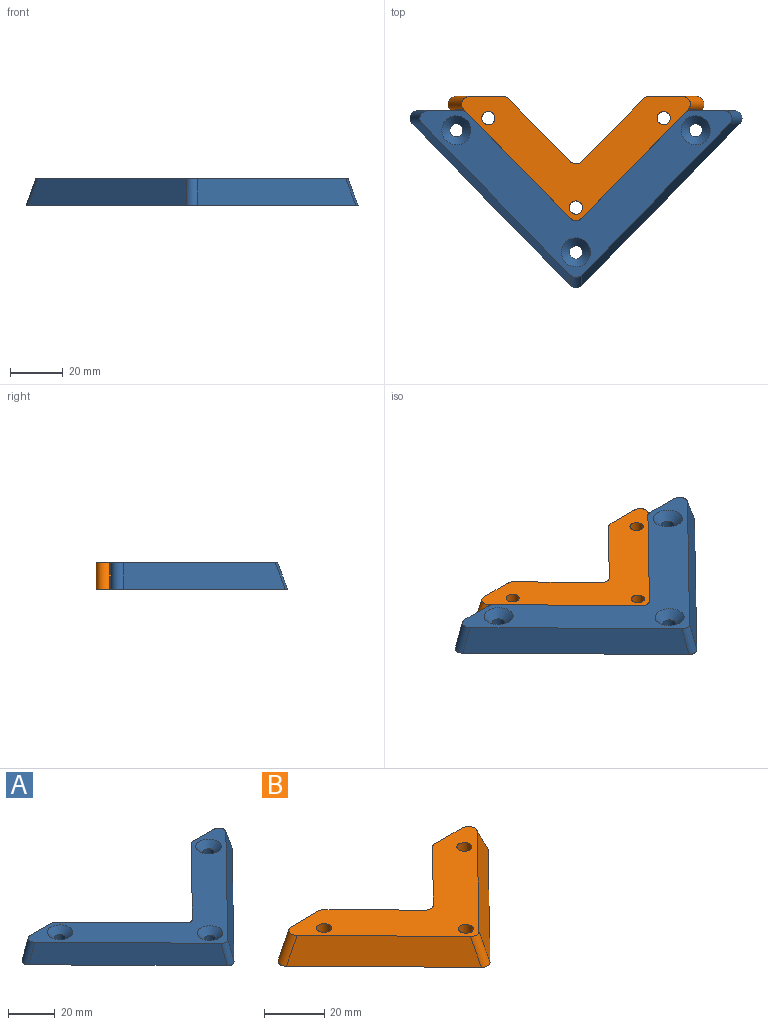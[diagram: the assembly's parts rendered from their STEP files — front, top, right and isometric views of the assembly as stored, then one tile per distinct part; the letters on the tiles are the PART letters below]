
ASSEMBLY  parts=2 mates=1
PART A: 20 faces, bbox 125.3x66.9x12.1 mm
  f0: plane 44.97x44.07mm, normal (-0.67,0.66,-0.34), area 631.3mm2, adj f9,f10,f14,f19
  f1: plane 44.97x44.07mm, normal (0.67,0.66,-0.34), area 631.3mm2, adj f9,f10,f14,f15
  f2: plane 15.93x10mm, normal (0,1,0), area 115.1mm2, adj f9,f10,f15,f16
  f3: plane 60.98x59.75mm, normal (-0.69,-0.68,0.26), area 856.1mm2, adj f9,f10,f16,f17
  f4: plane 60.98x59.75mm, normal (0.69,-0.68,0.26), area 856.1mm2, adj f9,f10,f17,f18
  f5: cylinder r=2.5mm len=7mm, axis (0,0,-1), area 110mm2, adj f10,f13
  f6: cylinder r=2.5mm len=7mm, axis (0,0,-1), area 110mm2, adj f10,f12
  f7: cylinder r=2.5mm len=7mm, axis (0,0,-1), area 110mm2, adj f10,f11
  f8: plane 15.93x10mm, normal (0,1,0), area 115.1mm2, adj f9,f10,f18,f19
  f9: plane 117.82x63.06mm, normal (0,0,1), area 1942.8mm2, adj f0,f1,f2,f3,f4,f8,f11,f12
  f10: plane 125.32x66.89mm, normal (0,0,-1), area 2202.4mm2, adj f0,f1,f2,f3,f4,f5,f6,f7
  f11: cone r=5.5mm half-angle=45deg, axis (0,0,1), area 106.6mm2, adj f7,f9
  f12: cone r=2.5mm half-angle=45deg, axis (0,0,1), area 106.6mm2, adj f6,f9
  f13: cone r=2.5mm half-angle=45deg, axis (0,0,1), area 106.6mm2, adj f5,f9
  f14: cylinder r=3mm len=10.72mm, axis (0,0.46,0.89), area 49.8mm2, adj f0,f1,f9,f10
  f15: cylinder r=3mm len=12.05mm, axis (0.45,0,0.89), area 28.7mm2, adj f1,f2,f9,f10
  f16: cylinder r=3mm len=12.11mm, axis (0.35,0,0.94), area 74.1mm2, adj f2,f3,f9,f10
  f17: cylinder r=3mm len=10.59mm, axis (0,-0.36,-0.93), area 48.9mm2, adj f3,f4,f9,f10
  f18: cylinder r=3mm len=12.11mm, axis (0.35,0,-0.94), area 74.1mm2, adj f4,f8,f9,f10
  f19: cylinder r=3mm len=12.05mm, axis (0.45,0,-0.89), area 28.7mm2, adj f0,f8,f9,f10
PART B: 20 faces, bbox 96.6x52.2x12.7 mm
  f0: plane 86.41x47.04mm, normal (0,0,1), area 1494.5mm2, adj f2,f3,f4,f5,f6,f7,f8,f9
  f1: plane 96.6x52.24mm, normal (0,0,-1), area 1570.9mm2, adj f2,f3,f4,f5,f6,f7,f11,f12
  f2: plane 27.53x26.98mm, normal (-0.69,0.68,-0.26), area 371.3mm2, adj f0,f1,f14,f19
  f3: plane 27.53x26.98mm, normal (0.69,0.68,-0.26), area 371.3mm2, adj f0,f1,f14,f15
  f4: plane 17.28x10mm, normal (0,1,0), area 128.5mm2, adj f0,f1,f15,f16
  f5: plane 46.39x45.46mm, normal (-0.67,-0.66,0.34), area 652.4mm2, adj f0,f1,f16,f17
  f6: plane 46.39x45.46mm, normal (0.67,-0.66,0.34), area 652.4mm2, adj f0,f1,f17,f18
  f7: plane 17.28x10mm, normal (0,1,0), area 128.5mm2, adj f0,f1,f18,f19
  f8: cylinder r=2.5mm len=7mm, axis (0,0,-1), area 110mm2, adj f0,f11
  f9: cylinder r=2.5mm len=7mm, axis (0,0,-1), area 110mm2, adj f0,f12
  f10: cylinder r=2.5mm len=7mm, axis (0,0,-1), area 110mm2, adj f0,f13
  f11: cone r=5.5mm half-angle=45deg, axis (0,0,-1), area 106.6mm2, adj f1,f8
  f12: cone r=2.5mm half-angle=45deg, axis (0,0,-1), area 106.6mm2, adj f1,f9
  f13: cone r=2.5mm half-angle=45deg, axis (0,0,-1), area 106.6mm2, adj f1,f10
  f14: cylinder r=3mm len=10.59mm, axis (0,0.36,0.93), area 48.9mm2, adj f0,f1,f2,f3
  f15: cylinder r=3mm len=11.55mm, axis (0.35,0,0.94), area 26.5mm2, adj f0,f1,f3,f4
  f16: cylinder r=3mm len=12.73mm, axis (0.45,0,0.89), area 77.1mm2, adj f0,f1,f4,f5
  f17: cylinder r=3mm len=10.72mm, axis (0,-0.46,-0.89), area 49.8mm2, adj f0,f1,f5,f6
  f18: cylinder r=3mm len=12.73mm, axis (0.45,0,-0.89), area 77.1mm2, adj f0,f1,f6,f7
  f19: cylinder r=3mm len=11.55mm, axis (0.35,0,-0.94), area 26.5mm2, adj f0,f1,f2,f7
PLACE A t=(-11.06,-32.47,-20.34)mm
PLACE B t=(-11.06,-11.04,-20.34)mm
MATE fastened B.f1 <-> A.f10  axis (0,0,-1) through (-13.07,-35.61,-20.34)mm
